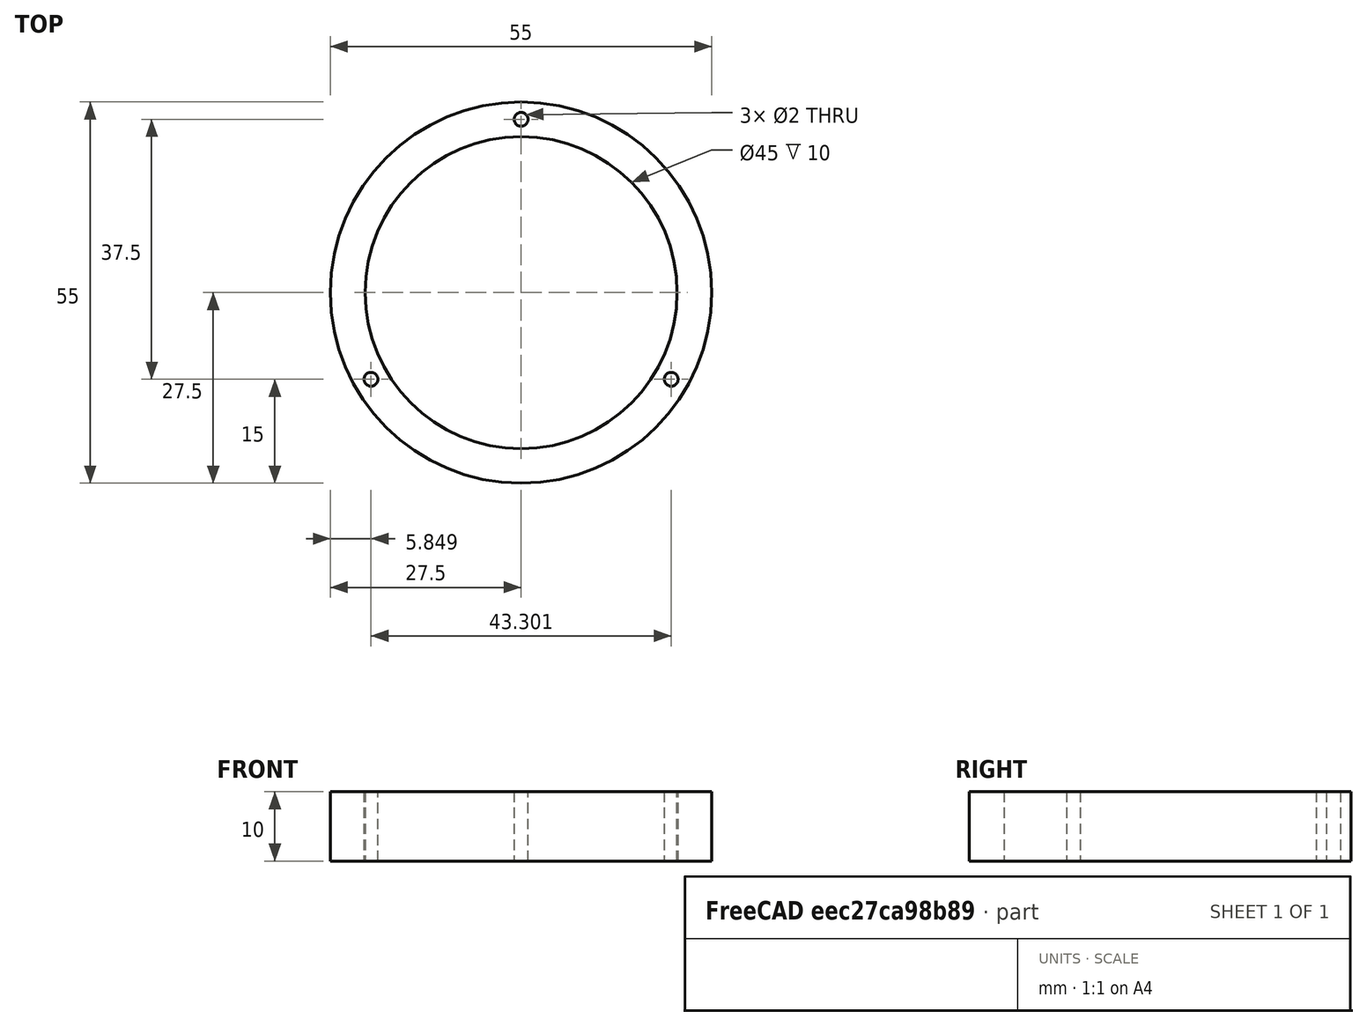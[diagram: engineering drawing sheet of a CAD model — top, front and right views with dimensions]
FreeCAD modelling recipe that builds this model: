
FCSTD DOCUMENT  (FreeCAD 0.19R24276 (Git))
Label: Ring_d45_d55
License: All rights reserved
LicenseURL: http://en.wikipedia.org/wiki/All_rights_reserved
objects: Sketcher::SketchObject×1, PartDesign::Pad×1, PartDesign::Body×1
note: 4 computed .brp shape members not serialized (recipe doc carries the construction recipe); baked Part::Feature solids carry a one-line shape summary decoded from their .brp

FEATURE [Sketcher::SketchObject] Sketch  label="Sketch_d45_d55"
  FullyConstrained = true
  MapMode = 5
  Support = -> [XY_Plane]
  sketch-geometry (9):
    g0: Circle CenterX=0 CenterY=0 CenterZ=0 NormalX=0 NormalY=0 NormalZ=1 AngleXU=0 Radius=22.5
    g1: Circle CenterX=0 CenterY=0 CenterZ=0 NormalX=0 NormalY=0 NormalZ=1 AngleXU=0 Radius=27.5
    g2: LineSegment StartX=0 StartY=25 StartZ=0 EndX=-21.6506 EndY=-12.5 EndZ=0
    g3: LineSegment StartX=-21.6506 StartY=-12.5 StartZ=0 EndX=21.6506 EndY=-12.5 EndZ=0
    g4: LineSegment StartX=21.6506 StartY=-12.5 StartZ=0 EndX=0 EndY=25 EndZ=0
    g5: Circle CenterX=0 CenterY=0 CenterZ=0 NormalX=0 NormalY=0 NormalZ=1 AngleXU=0 Radius=25
    g6: Circle CenterX=0 CenterY=25 CenterZ=0 NormalX=0 NormalY=0 NormalZ=1 AngleXU=0 Radius=1
    g7: Circle CenterX=-21.6506 CenterY=-12.5 CenterZ=0 NormalX=0 NormalY=0 NormalZ=1 AngleXU=0 Radius=1
    g8: Circle CenterX=21.6506 CenterY=-12.5 CenterZ=0 NormalX=0 NormalY=0 NormalZ=1 AngleXU=0 Radius=1
  constraints (21):
    c: Coincident(g0,g-1)
    c: Coincident(g1,g0)
    c: Diameter(g1) = 55
    c: Diameter(g0) = 45
    c: Coincident(g2,g3)
    c: Coincident(g3,g4)
    c: Coincident(g4,g2)
    c: Equal(g2,g3)
    c: Equal(g2,g4)
    c: PointOnObject(g2,g5)
    c: PointOnObject(g3,g5)
    c: PointOnObject(g4,g5)
    c: Coincident(g5,g0)
    c: PointOnObject(g4,g-2)
    c: Diameter(g5) = 50
    c: Coincident(g6,g2)
    c: Coincident(g7,g2)
    c: Coincident(g8,g3)
    c: Diameter(g8) = 2
    c: Equal(g8,g7)
    c: Equal(g8,g6)
FEATURE [PartDesign::Pad] Pad  label="Pad_h10"
  Direction = (1,1,1)
  Length = 10
  Length2 = 100
  Profile = -> Sketch
  Type = 0
FEATURE [PartDesign::Body] Body
  Group = -> [Sketch,Pad]
  Origin = -> Origin
  Tip = -> Pad
